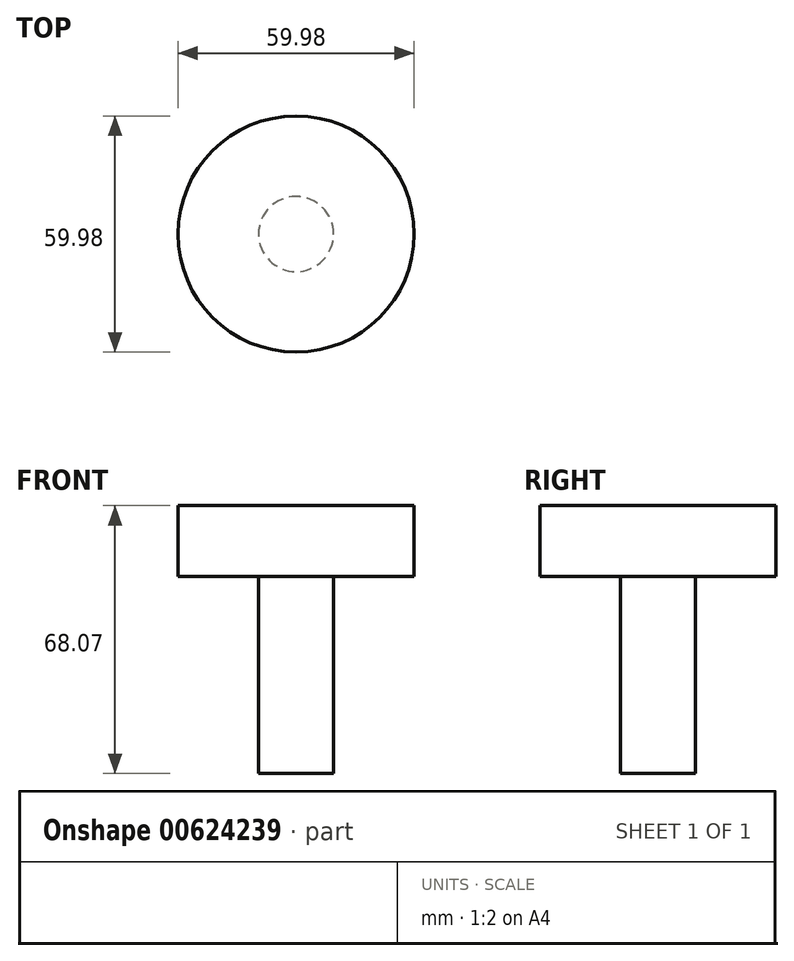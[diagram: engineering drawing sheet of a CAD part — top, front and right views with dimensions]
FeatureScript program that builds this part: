
annotation { "Feature Type Name" : "Feature", "Feature Type Description" : "" }
export const myFeature = defineFeature(function(context is Context, id is Id, definition is map)
    precondition{}
    {
        {
            var Q0;
            Q0=qCreatedBy(makeId("Top.planeOp"),FACE);
            var sketch = newSketch(context, id + "F0", { "sketchPlane" : qUnion([Q0])});
            skCircle(sketch, "E0", {"center": v(0, 0) * mm, "radius": 29.99 * mm});
            skSolve(sketch);
        }
        {
            var Q0;
            Q0=makeQuery(id+"F0.imprint","IMPRINT",FACE,{"disambiguationData":[TD([[makeQuery(id+"F0.imprint","IMPRINT",EDGE,{"derivedFrom":sQuery(id+"F0.wireOp",EDGE,"E0")}),1.0]])]});
            extrude(context, id + "F1", {"entities" : qUnion([Q0]), "depth" : 18.03 * mm, "offsetDistance" : 25.4 * mm});
        }
        {
            var Q0;
            Q0=makeQuery(id+"F1.opExtrude","CAP_FACE",FACE,{"disambiguationData":[OSD([sQuery(id+"F0.wireOp",EDGE,"E0")])],"isStart":false});
            var sketch = newSketch(context, id + "F2", { "sketchPlane" : qUnion([Q0])});
            skCircle(sketch, "E1", {"center": v(0, 0) * mm, "radius": 9.53 * mm});
            skSolve(sketch);
        }
        {
            var Q0;
            Q0=makeQuery(id+"F2.imprint","IMPRINT",FACE,{"disambiguationData":[TD([[makeQuery(id+"F2.imprint","IMPRINT",EDGE,{"derivedFrom":sQuery(id+"F2.wireOp",EDGE,"E1")}),1.0]])]});
            extrude(context, id + "F3", {"entities" : qUnion([Q0]), "operationType" : NewBodyOperationType.ADD, "oppositeDirection" : true, "depth" : 68.07 * mm, "offsetDistance" : 25.4 * mm});
        }
    });
